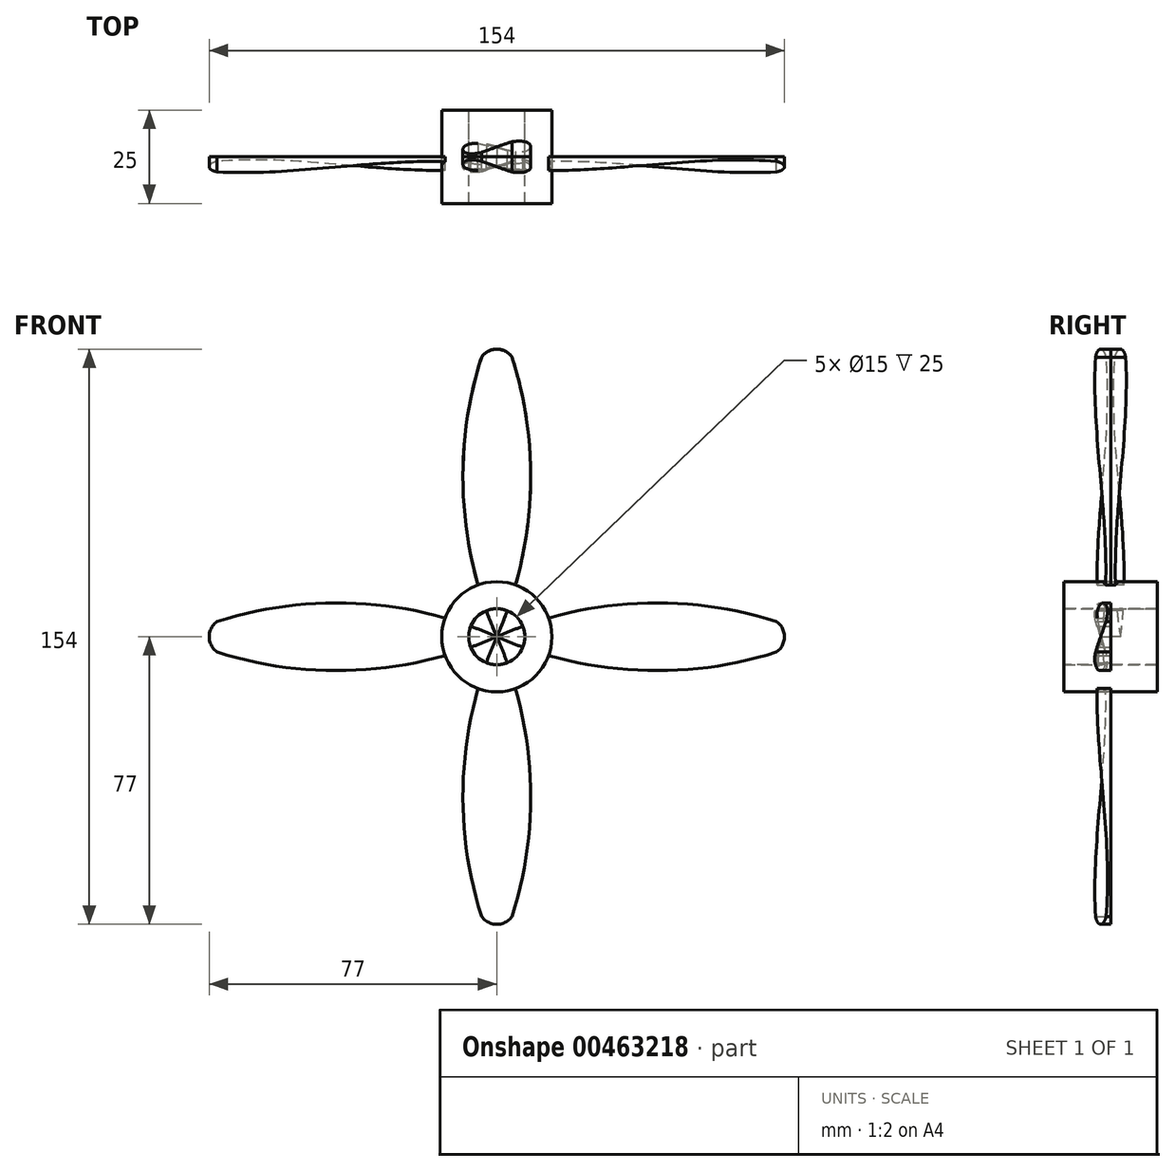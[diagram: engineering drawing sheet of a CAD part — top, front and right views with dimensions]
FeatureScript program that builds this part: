
annotation { "Feature Type Name" : "Feature", "Feature Type Description" : "" }
export const myFeature = defineFeature(function(context is Context, id is Id, definition is map)
    precondition{}
    {
        {
            var Q0;
            Q0=qCreatedBy(makeId("Top.planeOp"),FACE);
            cPlane(context, id + "F0", {"entities" : qUnion([Q0]), "cplaneType" : CPlaneType.OFFSET, "offset" : 77 * mm, "width" : 150 * mm, "height" : 150 * mm});
        }
        {
            var Q0;
            Q0=qCreatedBy(makeId("Top.planeOp"),FACE);
            var sketch = newSketch(context, id + "F1", { "sketchPlane" : qUnion([Q0])});
            skLineSegment(sketch, "E0", {"start": v(-37.69, 0) * mm, "end": v(38.78, 0) * mm, "construction": true});
            skLineSegment(sketch, "E1", {"start": v(0, 37.14) * mm, "end": v(0, -34.53) * mm, "construction": true});
            skLineSegment(sketch, "E2", {"start": v(-24.35, -6.2) * mm, "end": v(-22.64, -10.9) * mm});
            skLineSegment(sketch, "E3", {"start": v(-22.64, -10.9) * mm, "end": v(24.35, 6.2) * mm});
            skLineSegment(sketch, "E4", {"start": v(24.35, 6.2) * mm, "end": v(22.64, 10.9) * mm});
            skLineSegment(sketch, "E5", {"start": v(22.64, 10.9) * mm, "end": v(-24.35, -6.2) * mm});
            skLineSegment(sketch, "E6", {"start": v(-23.5, -8.55) * mm, "end": v(23.5, 8.55) * mm, "construction": true});
            skLineSegment(sketch, "E7", {"start": v(0.86, -2.35) * mm, "end": v(-0.86, 2.35) * mm, "construction": true});
            skSolve(sketch);
        }
        {
            var Q0;
            Q0=qCreatedBy(id+"F0.planeOp",FACE);
            var sketch = newSketch(context, id + "F2", { "sketchPlane" : qUnion([Q0])});
            skLineSegment(sketch, "E8", {"start": v(-22.64, 10.9) * mm, "end": v(24.35, -6.2) * mm});
            skLineSegment(sketch, "E9", {"start": v(-22.64, 10.9) * mm, "end": v(-24.35, 6.2) * mm});
            skLineSegment(sketch, "E10", {"start": v(-24.35, 6.2) * mm, "end": v(22.64, -10.9) * mm});
            skLineSegment(sketch, "E11", {"start": v(22.64, -10.9) * mm, "end": v(24.35, -6.2) * mm});
            skLineSegment(sketch, "E12", {"start": v(-23.5, 8.55) * mm, "end": v(23.5, -8.55) * mm, "construction": true});
            skLineSegment(sketch, "E13", {"start": v(-0.86, -2.35) * mm, "end": v(0.86, 2.35) * mm, "construction": true});
            skSolve(sketch);
        }
        {
            var Q0;
            Q0=makeQuery(id+"F1.imprint","IMPRINT",FACE,{"disambiguationData":[TD([[makeQuery(id+"F1.imprint","IMPRINT",EDGE,{"derivedFrom":sQuery(id+"F1.wireOp",EDGE,"E2")}),1.0]])]});
            var Q1;
            Q1=makeQuery(id+"F2.imprint","IMPRINT",FACE,{"disambiguationData":[TD([[makeQuery(id+"F2.imprint","IMPRINT",EDGE,{"derivedFrom":sQuery(id+"F2.wireOp",EDGE,"E8")}),-1.0]])]});
            loft(context, id + "F3", {"sheetProfilesArray" : [{ "sheetProfileEntities" : qUnion([Q0]) }, { "sheetProfileEntities" : qUnion([Q1]) }]});
        }
        {
            var Q0;
            Q0=qCreatedBy(makeId("Front.planeOp"),FACE);
            var sketch = newSketch(context, id + "F4", { "sketchPlane" : qUnion([Q0])});
            skLineSegment(sketch, "E14", {"start": v(0, 0) * mm, "end": v(0, 144) * mm, "construction": true});
            skArc(sketch, "E15", {"start": v(-4.1, 74.86) * mm, "mid": v(-8.9, 37.05) * mm, "end": v(0, 0) * mm});
            skArc(sketch, "E16.MirrorCS", {"start": v(4.1, 74.86) * mm, "mid": v(8.9, 37.05) * mm, "end": v(0, 0) * mm});
            skArc(sketch, "E17", {"start": v(4.1, 74.86) * mm, "mid": v(0, 77) * mm, "end": v(-4.1, 74.86) * mm});
            skLineSegment(sketch, "E18", {"start": v(-55.49, 0) * mm, "end": v(60.98, 0) * mm, "construction": true});
            skLineSegment(sketch, "E19", {"start": v(-26.32, -26.32) * mm, "end": v(45.74, 45.74) * mm, "construction": true});
            skSolve(sketch);
        }
        {
            var Q0;
            Q0 = qSketchRegion(id + "F4", true);
            extrude(context, id + "F5", {"entities" : qUnion([Q0]), "operationType" : NewBodyOperationType.INTERSECT, "depth" : 25 * mm});
        }
        {
            var Q0;
            Q0=qCreatedBy(makeId("Front.planeOp"),FACE);
            var sketch = newSketch(context, id + "F6", { "sketchPlane" : qUnion([Q0])});
            skCircle(sketch, "E20", {"center": v(0, 0) * mm, "radius": 7.5 * mm});
            skCircle(sketch, "E21", {"center": v(0, 0) * mm, "radius": 14.75 * mm});
            skSolve(sketch);
        }
        {
            var Q0;
            Q0=makeQuery(id+"F6.imprint","IMPRINT",FACE,{"disambiguationData":[TD([[makeQuery(id+"F6.imprint","IMPRINT",EDGE,{"derivedFrom":sQuery(id+"F6.wireOp",EDGE,"E20")}),-1.0]])]});
            extrude(context, id + "F7", {"entities" : qUnion([Q0]), "operationType" : NewBodyOperationType.ADD, "endBound" : BoundingType.SYMMETRIC, "depth" : 25 * mm});
        }
        {
            var Q0;
            Q0=makeQuery(id+"F3.opLoft","SWEPT_BODY",BODY,{"disambiguationData":[OSD([makeQuery(id+"F1.imprint","IMPRINT",FACE,{"disambiguationData":[TD([[makeQuery(id+"F1.imprint","IMPRINT",EDGE,{"derivedFrom":sQuery(id+"F1.wireOp",EDGE,"E2")}),1.0]])]}),makeQuery(id+"F2.imprint","IMPRINT",FACE,{"disambiguationData":[TD([[makeQuery(id+"F2.imprint","IMPRINT",EDGE,{"derivedFrom":sQuery(id+"F2.wireOp",EDGE,"E8")}),-1.0]])]})])]});
            var Q1;
            Q1=makeQuery(id+"F7.opExtrude","CAP_EDGE",EDGE,{"disambiguationData":[OSD([sQuery(id+"F6.wireOp",EDGE,"E20")])],"isStart":false});
            circularPattern(context, id + "F8", {"entities" : qUnion([Q0]), "axis" : qUnion([Q1]), "angle" : 360 * degree, "instanceCount" : 4, "equalSpace" : true});
        }
        {
            var Q0;
            Q0=makeQuery(id+"F3.opLoft","SWEPT_BODY",BODY,{"disambiguationData":[OSD([makeQuery(id+"F1.imprint","IMPRINT",FACE,{"disambiguationData":[TD([[makeQuery(id+"F1.imprint","IMPRINT",EDGE,{"derivedFrom":sQuery(id+"F1.wireOp",EDGE,"E2")}),1.0]])]}),makeQuery(id+"F2.imprint","IMPRINT",FACE,{"disambiguationData":[TD([[makeQuery(id+"F2.imprint","IMPRINT",EDGE,{"derivedFrom":sQuery(id+"F2.wireOp",EDGE,"E8")}),-1.0]])]})])]});
            var Q1;
            Q1=qCreatedBy(makeId("Front.planeOp"),FACE);
            mirror(context, id + "F9", {"entities" : qUnion([Q0]), "mirrorPlane" : qUnion([Q1])});
        }
    });
